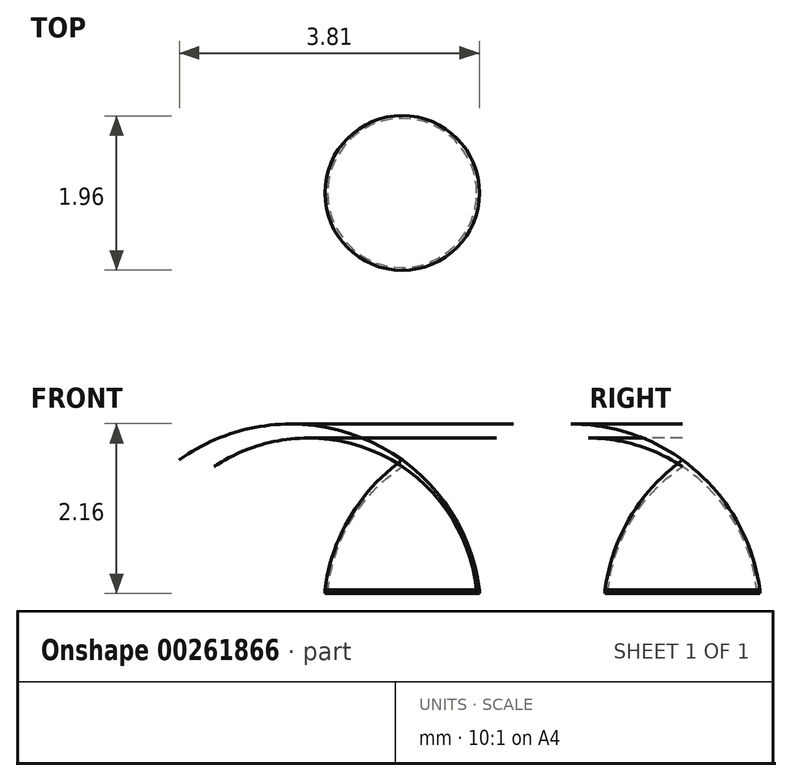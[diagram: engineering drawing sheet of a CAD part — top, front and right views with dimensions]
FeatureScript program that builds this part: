
annotation { "Feature Type Name" : "Feature", "Feature Type Description" : "" }
export const myFeature = defineFeature(function(context is Context, id is Id, definition is map)
    precondition{}
    {
        {
            var Q0;
            Q0=qCreatedBy(makeId("Top.planeOp"),FACE);
            var sketch = newSketch(context, id + "F0", { "sketchPlane" : qUnion([Q0])});
            skCircle(sketch, "E0", {"center": v(0, 0) * mm, "radius": 4.1 * mm});
            skSolve(sketch);
        }
        {
            var Q0;
            Q0=qCreatedBy(makeId("Right.planeOp"),FACE);
            var sketch = newSketch(context, id + "F1", { "sketchPlane" : qUnion([Q0])});
            skArc(sketch, "E1", {"start": v(0, 7.18) * mm, "mid": v(-2.8, 4.12) * mm, "end": v(-4.15, 0.2) * mm});
            skLineSegment(sketch, "E2", {"start": v(-4.15, 0) * mm, "end": v(-4.15, 0.2) * mm});
            skLineSegment(sketch, "E3", {"start": v(0, 7.18) * mm, "end": v(0, 6.82) * mm});
            skArc(sketch, "E4", {"start": v(0, 6.82) * mm, "mid": v(-2.78, 3.87) * mm, "end": v(-4, 0) * mm});
            skLineSegment(sketch, "E5", {"start": v(-4.15, 0) * mm, "end": v(-4, 0) * mm});
            skSolve(sketch);
        }
        {
            var Q0;
            Q0=makeQuery(id+"F1.imprint","IMPRINT",FACE,{"disambiguationData":[TD([[makeQuery(id+"F1.imprint","IMPRINT",EDGE,{"derivedFrom":sQuery(id+"F1.wireOp",EDGE,"E1")}),1.0]])]});
            var Q1;
            Q1=sQuery(id+"F0.wireOp",EDGE,"E0");
            revolve(context, id + "F2", {"entities" : qUnion([Q0]), "axis" : qUnion([Q1]), "revolveType" : RevolveType.FULL});
        }
        {
            var Q0;
            Q0=makeQuery(id+"F2.opRevolve","SWEPT_BODY",BODY,{"disambiguationData":[OSD([sQuery(id+"F1.wireOp",EDGE,"E1"),sQuery(id+"F1.wireOp",EDGE,"E2"),sQuery(id+"F1.wireOp",EDGE,"E3"),sQuery(id+"F1.wireOp",EDGE,"E4"),sQuery(id+"F1.wireOp",EDGE,"E5")])]});
            var Q1;
            Q1=sQuery(id+"F0.wireOp",VERTEX,"E0.center");
            transform(context, id + "F3", {"entities" : qUnion([Q0]), "transformType" : TransformType.SCALE_UNIFORMLY, "scale" : 0.24, "scalePoint" : qUnion([Q1]), "makeCopy" : false});
        }
    });
